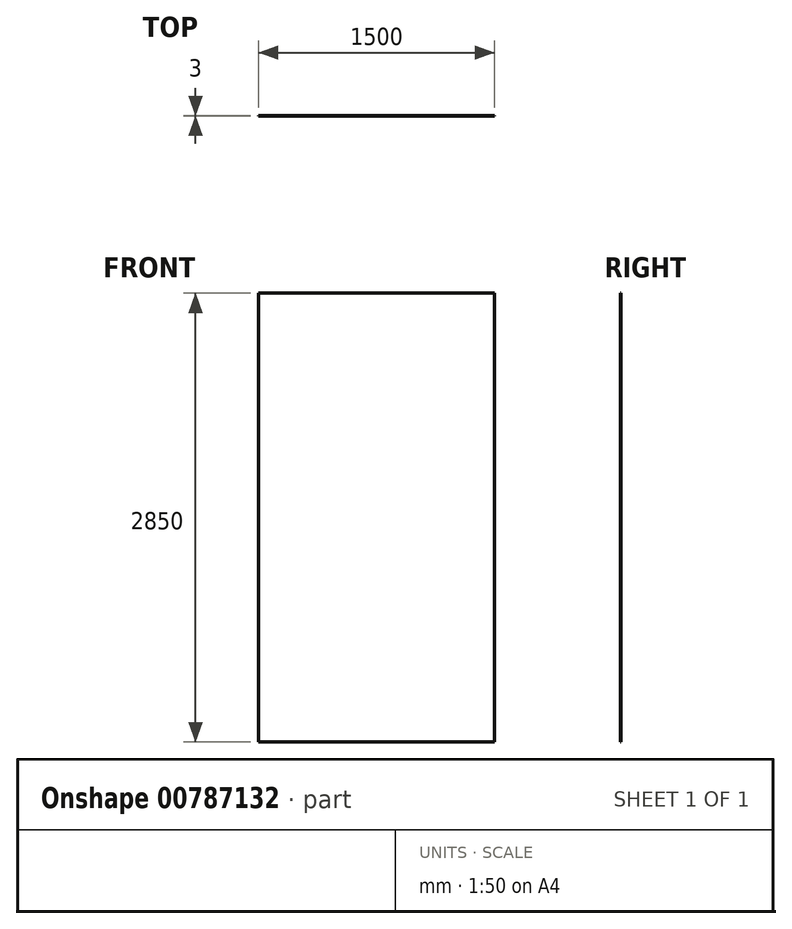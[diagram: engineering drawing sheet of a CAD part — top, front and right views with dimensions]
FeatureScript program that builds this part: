
annotation { "Feature Type Name" : "Feature", "Feature Type Description" : "" }
export const myFeature = defineFeature(function(context is Context, id is Id, definition is map)
    precondition{}
    {
        {
            var Q0;
            Q0=qCreatedBy(makeId("Front.planeOp"),FACE);
            var sketch = newSketch(context, id + "F0", { "sketchPlane" : qUnion([Q0])});
            skLineSegment(sketch, "E0.bottom", {"start": v(750, 1425) * mm, "end": v(-750, 1425) * mm});
            skLineSegment(sketch, "E0.top", {"start": v(750, -1425) * mm, "end": v(-750, -1425) * mm});
            skLineSegment(sketch, "E0.left", {"start": v(750, 1425) * mm, "end": v(750, -1425) * mm});
            skLineSegment(sketch, "E0.right", {"start": v(-750, 1425) * mm, "end": v(-750, -1425) * mm});
            skPoint(sketch, "E0.middle", {"position": v(0, 0) * mm});
            skSolve(sketch);
        }
        {
            var Q0;
            Q0=makeQuery(id+"F0.imprint","IMPRINT",FACE,{"disambiguationData":[TD([[makeQuery(id+"F0.imprint","IMPRINT",EDGE,{"derivedFrom":sQuery(id+"F0.wireOp",EDGE,"E0.bottom")}),1.0]])]});
            extrude(context, id + "F1", {"entities" : qUnion([Q0]), "depth" : 3 * mm, "offsetDistance" : 25 * mm});
        }
    });
